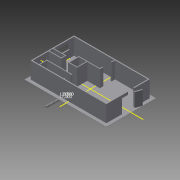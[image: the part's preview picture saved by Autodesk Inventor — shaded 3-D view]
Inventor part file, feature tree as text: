
AUTODESK INVENTOR PART (.ipt)
format: ipt  version: 2013 SP2 (Build 170200200, 200)  size: 617,984 bytes
history: native  units: in
note: dims shown in document units (in); Inventor stores cm internally (conversion verified against a paired STEP export)
features: extrude x23, sketch x17, projected_geometry x9
ambient origin geometry x8: Origin, YZ Plane, XZ Plane, XY Plane, X Axis, Y Axis, Z Axis, Center Point
feature tree (49):
  extrude  "Extrusion7"  Depth=5.0in
  extrude  "Extrusion8"  Depth=72.0in
  sketch  "Sketch5"  dims[d57=4.5in d58=60.0in d61=54.0in d64=432.0in]
  extrude  "Extrusion9"  Depth=432.0in
  extrude  "Extrusion10"  Depth=41.0in
  extrude  "Extrusion11"  Depth=93.0in
  extrude  "Extrusion12"  Depth=4.5in
  extrude  "Extrusion14"  Depth=73.0in
  extrude  "Extrusion16"  Depth=6.0in
  extrude  "Extrusion15"  Depth=73.0in
  extrude  "Extrusion17"  Depth=4.5in
  sketch  "Sketch13"  dims[d104=39.0in d105=4.5in]
  extrude  "Extrusion23"  Depth=4.5in
  extrude  "Extrusion24"  Depth=4.5in
  extrude  "Extrusion25"  Depth=48.0in
  extrude  "Extrusion26"  Depth=240.0in
  extrude  "Extrusion27"  Depth=90.0in
  extrude  "Extrusion28"  Depth=4.5in
  extrude  "Extrusion29"  Depth=252.0in
  extrude  "Extrusion31"  Depth=6.0in
  extrude  "Extrusion18"  Depth=46.0in
  extrude  "Extrusion19"  Depth=41.0in
  extrude  "Extrusion20"  Depth=4.5in
  sketch  "Sketch15"  dims[d106=4.5in d107=4.5in]
  extrude  "Extrusion21"  Depth=73.0in
  extrude  "Extrusion22"  Depth=93.0in
  sketch  "Sketch1"  dims[d1=240.0in d4=5.0in d5=6.0in]
  sketch  "Sketch4"  dims[d14=72.0in d30=72.0in d40=432.0in]
  projected_geometry  "Projected Loop3"
  projected_geometry  "Projected Loop4"
  sketch  "Sketch6"  dims[d88=6.0in d89=41.0in d90=248.0in]
  projected_geometry  "Projected Loop5"
  projected_geometry  "Projected Loop6"
  sketch  "Sketch7"  dims[d91=37.0in d92=93.0in d93=117.0in]
  sketch  "Sketch9"  dims[d94=4.5in d95=4.5in]
  sketch  "Sketch10"  dims[d96=4.5in d97=73.0in]
  projected_geometry  "Projected Loop7"
  sketch  "Sketch11"  dims[d98=46.0in d99=36.0in d100=6.0in]
  sketch  "Sketch12"  dims[d102=37.0in d103=73.0in]
  projected_geometry  "Projected Loop8"
  sketch  "Sketch16"  dims[d108=4.5in d109=4.5in]
  projected_geometry  "Projected Loop13"
  projected_geometry  "Projected Loop14"
  projected_geometry  "Projected Loop15"
  sketch  "Sketch17"  dims[d110=263.0in d112=48.0in]
  sketch  "Sketch18"  dims[d117=45.5in d119=240.0in d120=6.0in]
  sketch  "Sketch19"  dims[d122=117.0in d123=90.0in]
  sketch  "Sketch20"  dims[d124=234.0in d125=4.5in]
  sketch  "Sketch21"  dims[d127=4.5in d128=252.0in d129=6.0in d130=46.0in d131=41.0in d132=4.5in d133=73.0in d134=93.0in d135=428.0in d136=97.0in d137=0.0in d138=1.0in d139=0.0in d140=80.0in d142=9.0in d143=32.0in d144=78.0in d145=28.0in d146=2.0in d147=2.0in d148=0.0in d149=1.0in d150=0.0in d151=16.0in d152=0.0in d153=66.0in d155=36.0in d156=43.0in d157=25.5in d158=16.0in d159=0.0in d192=35.0in d193=6.0in d195=35.0in d196=0.0in d197=7.25in d198=7.5in d199=7.25in d200=7.5in d201=7.25in d202=7.5in d203=7.25in d204=7.5in d205=7.25in d206=7.5in d207=7.25in d208=7.5in d209=7.25in d210=7.5in d211=7.25in d212=7.5in d213=7.25in d214=7.5in d215=7.25in d216=7.5in d217=7.25in d218=7.5in d219=7.25in d220=7.5in d221=7.25in d222=7.25in d223=7.5in d224=7.5in d225=7.5in d226=7.25in d227=35.0in d228=0.0in d230=1.0in d232=1.0in d233=0.0in d236=84.0in d237=20.25in d238=4.5in d240=0.001in d241=0.0in d252=17.0in d253=17.0in d256=8.5in d312=3.0in d313=0.0in d314=2.0in d315=0.0in d316=1.0in d317=0.0in d318=12.0in d319=17.0in d320=17.0in d321=8.5in d322=12.0in d323=17.0in d324=17.0in d325=8.5in d326=22.0in d327=22.0in d328=2.0in d329=0.0in d330=3.0in d331=0.0in d334=1.0in d335=0.0in d336=1.0in d337=0.0in d338=1.0in d339=0.0in d340=1.0in d341=0.0in d342=0.5in d343=0.0in d344=32.0in d346=4.5in d347=6.0in d348=36.0in d349=80.0in d350=0.0in d351=1.0in d352=0.0in d353=0.1374in d354=24.0in d355=24.0in d358=1.0in d359=0.0in]
